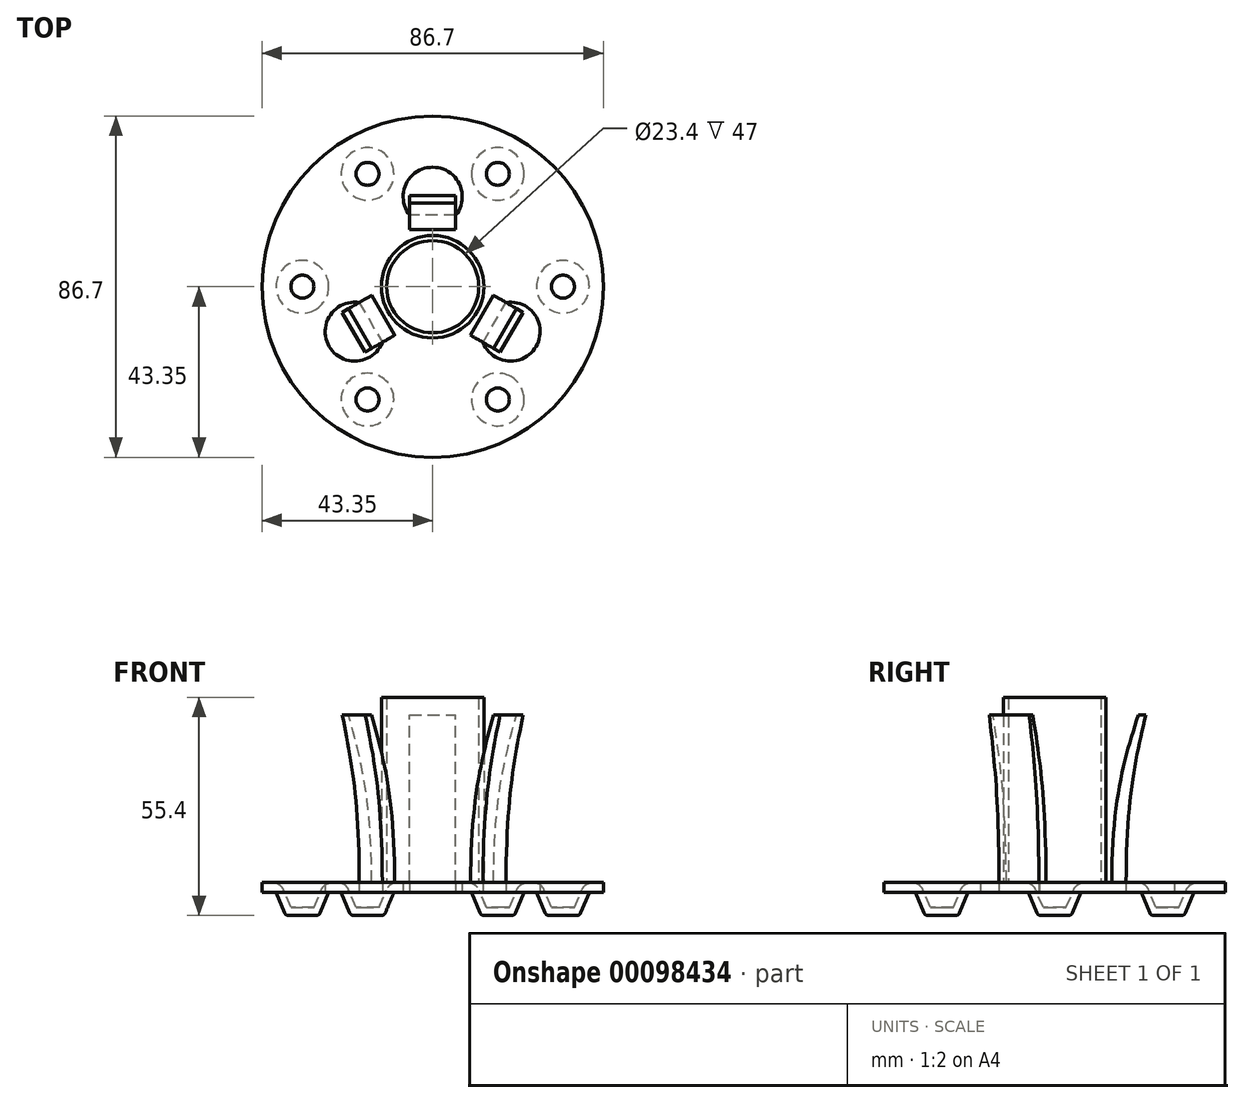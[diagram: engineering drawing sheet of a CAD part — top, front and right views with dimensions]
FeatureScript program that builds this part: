
annotation { "Feature Type Name" : "Feature", "Feature Type Description" : "" }
export const myFeature = defineFeature(function(context is Context, id is Id, definition is map)
    precondition{}
    {
        {
            var Q0;
            Q0=qCreatedBy(makeId("Top.planeOp"),FACE);
            var sketch = newSketch(context, id + "F0", { "sketchPlane" : qUnion([Q0])});
            skCircle(sketch, "E0", {"center": v(0, 0) * mm, "radius": 43.35 * mm});
            skCircle(sketch, "E1", {"center": v(-16.55, -28.67) * mm, "radius": 7.75 * mm});
            skCircle(sketch, "E2", {"center": v(-16.55, -28.67) * mm, "radius": 4.25 * mm});
            skCircle(sketch, "E3.1.0", {"center": v(16.55, -28.67) * mm, "radius": 4.25 * mm});
            skCircle(sketch, "E3.1.1", {"center": v(16.55, -28.67) * mm, "radius": 7.75 * mm});
            skCircle(sketch, "E3.2.0", {"center": v(33.1, 0) * mm, "radius": 4.25 * mm});
            skCircle(sketch, "E3.2.1", {"center": v(33.1, 0) * mm, "radius": 7.75 * mm});
            skCircle(sketch, "E3.3.0", {"center": v(16.55, 28.67) * mm, "radius": 4.25 * mm});
            skCircle(sketch, "E3.3.1", {"center": v(16.55, 28.67) * mm, "radius": 7.75 * mm});
            skCircle(sketch, "E3.4.0", {"center": v(-16.55, 28.67) * mm, "radius": 4.25 * mm});
            skCircle(sketch, "E3.4.1", {"center": v(-16.55, 28.67) * mm, "radius": 7.75 * mm});
            skCircle(sketch, "E3.5.0", {"center": v(-33.1, 0) * mm, "radius": 4.25 * mm});
            skCircle(sketch, "E3.5.1", {"center": v(-33.1, 0) * mm, "radius": 7.75 * mm});
            skCircle(sketch, "E4", {"center": v(19.79, -11.42) * mm, "radius": 7.5 * mm});
            skLineSegment(sketch, "E5", {"start": v(12.8, -14.14) * mm, "end": v(18.64, -4.01) * mm});
            skLineSegment(sketch, "E6", {"start": v(0, 0) * mm, "end": v(37.54, -21.67) * mm, "construction": true});
            skCircle(sketch, "E7.1.0", {"center": v(0, 22.85) * mm, "radius": 7.5 * mm});
            skLineSegment(sketch, "E7.1.1", {"start": v(5.84, 18.15) * mm, "end": v(-5.84, 18.15) * mm});
            skLineSegment(sketch, "E7.1.2", {"start": v(0, 0) * mm, "end": v(0, 43.35) * mm, "construction": true});
            skCircle(sketch, "E7.2.0", {"center": v(-19.79, -11.42) * mm, "radius": 7.5 * mm});
            skLineSegment(sketch, "E7.2.1", {"start": v(-18.64, -4.01) * mm, "end": v(-12.8, -14.14) * mm});
            skLineSegment(sketch, "E7.2.2", {"start": v(0, 0) * mm, "end": v(-37.54, -21.68) * mm, "construction": true});
            skCircle(sketch, "E8.0", {"center": v(-16.55, -28.67) * mm, "radius": 5.75 * mm});
            skCircle(sketch, "E9.1.0", {"center": v(16.55, -28.67) * mm, "radius": 5.75 * mm});
            skCircle(sketch, "E9.2.0", {"center": v(33.1, 0) * mm, "radius": 5.75 * mm});
            skCircle(sketch, "E9.3.0", {"center": v(16.55, 28.67) * mm, "radius": 5.75 * mm});
            skCircle(sketch, "E9.4.0", {"center": v(-16.55, 28.67) * mm, "radius": 5.75 * mm});
            skCircle(sketch, "E9.5.0", {"center": v(-33.1, 0) * mm, "radius": 5.75 * mm});
            skSolve(sketch);
        }
        {
            var Q0;
            Q0=makeQuery(id+"F0.imprint","IMPRINT",FACE,{"disambiguationData":[TD([[makeQuery(id+"F0.imprint","IMPRINT",EDGE,{"derivedFrom":sQuery(id+"F0.wireOp",EDGE,"E0")}),1.0]])]});
            var Q1;
            Q1=makeQuery(id+"F0.imprint","IMPRINT",FACE,{"disambiguationData":[TD([[makeQuery(id+"F0.imprint","IMPRINT",EDGE,{"derivedFrom":sQuery(id+"F0.wireOp",EDGE,"E3.5.1")}),1.0]])]});
            var Q2;
            Q2=makeQuery(id+"F0.imprint","IMPRINT",FACE,{"disambiguationData":[TD([[makeQuery(id+"F0.imprint","IMPRINT",EDGE,{"derivedFrom":sQuery(id+"F0.wireOp",EDGE,"E3.4.1")}),1.0]])]});
            var Q3;
            Q3=makeQuery(id+"F0.imprint","IMPRINT",FACE,{"disambiguationData":[TD([[makeQuery(id+"F0.imprint","IMPRINT",EDGE,{"derivedFrom":sQuery(id+"F0.wireOp",EDGE,"E3.3.1")}),1.0]])]});
            var Q4;
            {var subQ0=sQuery(id+"F0.wireOp",EDGE,"E7.1.1");Q4=makeQuery(id+"F0.imprint","IMPRINT",FACE,{"disambiguationData":[TD([[makeQuery(id+"F0.imprint","IMPRINT",EDGE,{"derivedFrom":subQ0}),1.0]])]});}
            var Q5;
            {var subQ0=sQuery(id+"F0.wireOp",EDGE,"E7.2.1");Q5=makeQuery(id+"F0.imprint","IMPRINT",FACE,{"disambiguationData":[TD([[makeQuery(id+"F0.imprint","IMPRINT",EDGE,{"derivedFrom":subQ0}),1.0]])]});}
            var Q6;
            {var subQ0=sQuery(id+"F0.wireOp",EDGE,"E5");Q6=makeQuery(id+"F0.imprint","IMPRINT",FACE,{"disambiguationData":[TD([[makeQuery(id+"F0.imprint","IMPRINT",EDGE,{"derivedFrom":subQ0}),1.0]])]});}
            var Q7;
            Q7=makeQuery(id+"F0.imprint","IMPRINT",FACE,{"disambiguationData":[TD([[makeQuery(id+"F0.imprint","IMPRINT",EDGE,{"derivedFrom":sQuery(id+"F0.wireOp",EDGE,"E3.2.1")}),1.0]])]});
            var Q8;
            Q8=makeQuery(id+"F0.imprint","IMPRINT",FACE,{"disambiguationData":[TD([[makeQuery(id+"F0.imprint","IMPRINT",EDGE,{"derivedFrom":sQuery(id+"F0.wireOp",EDGE,"E3.1.1")}),1.0]])]});
            var Q9;
            Q9=makeQuery(id+"F0.imprint","IMPRINT",FACE,{"disambiguationData":[TD([[makeQuery(id+"F0.imprint","IMPRINT",EDGE,{"derivedFrom":sQuery(id+"F0.wireOp",EDGE,"E1")}),1.0]])]});
            extrude(context, id + "F1", {"entities" : qUnion([Q0, Q1, Q2, Q3, Q4, Q5, Q6, Q7, Q8, Q9]), "depth" : 2.54 * mm});
        }
        {
            var Q0;
            Q0=makeQuery(id+"F1.opExtrude","CAP_FACE",FACE,{"disambiguationData":[OSD([sQuery(id+"F0.wireOp",EDGE,"E0"),sQuery(id+"F0.wireOp",EDGE,"E4"),sQuery(id+"F0.wireOp",EDGE,"E5"),sQuery(id+"F0.wireOp",EDGE,"E7.1.0"),sQuery(id+"F0.wireOp",EDGE,"E7.1.1"),sQuery(id+"F0.wireOp",EDGE,"E7.2.0"),sQuery(id+"F0.wireOp",EDGE,"E7.2.1"),sQuery(id+"F0.wireOp",EDGE,"E8.0"),sQuery(id+"F0.wireOp",EDGE,"E9.1.0"),sQuery(id+"F0.wireOp",EDGE,"E9.2.0"),sQuery(id+"F0.wireOp",EDGE,"E9.3.0"),sQuery(id+"F0.wireOp",EDGE,"E9.4.0"),sQuery(id+"F0.wireOp",EDGE,"E9.5.0")])],"isStart":false});
            cPlane(context, id + "F2", {"entities" : qUnion([Q0]), "cplaneType" : CPlaneType.OFFSET, "offset" : 0 * mm, "width" : 150 * mm, "height" : 150 * mm});
        }
        {
            var Q0;
            Q0=qCreatedBy(id+"F2.planeOp",FACE);
            var sketch = newSketch(context, id + "F3", { "sketchPlane" : qUnion([Q0])});
            skCircle(sketch, "E10.0", {"center": v(-16.55, -28.67) * mm, "radius": 7.75 * mm});
            skSolve(sketch);
        }
        {
            var Q0;
            Q0=makeQuery(id+"F1.opExtrude","CAP_FACE",FACE,{"disambiguationData":[OSD([sQuery(id+"F0.wireOp",EDGE,"E0"),sQuery(id+"F0.wireOp",EDGE,"E4"),sQuery(id+"F0.wireOp",EDGE,"E5"),sQuery(id+"F0.wireOp",EDGE,"E7.1.0"),sQuery(id+"F0.wireOp",EDGE,"E7.1.1"),sQuery(id+"F0.wireOp",EDGE,"E7.2.0"),sQuery(id+"F0.wireOp",EDGE,"E7.2.1"),sQuery(id+"F0.wireOp",EDGE,"E8.0"),sQuery(id+"F0.wireOp",EDGE,"E9.1.0"),sQuery(id+"F0.wireOp",EDGE,"E9.2.0"),sQuery(id+"F0.wireOp",EDGE,"E9.3.0"),sQuery(id+"F0.wireOp",EDGE,"E9.4.0"),sQuery(id+"F0.wireOp",EDGE,"E9.5.0")])],"isStart":false});
            cPlane(context, id + "F4", {"entities" : qUnion([Q0]), "cplaneType" : CPlaneType.OFFSET, "offset" : 8.4 * mm, "oppositeDirection" : true, "width" : 150 * mm, "height" : 150 * mm});
        }
        {
            var Q0;
            Q0=qCreatedBy(id+"F4.planeOp",FACE);
            var sketch = newSketch(context, id + "F5", { "sketchPlane" : qUnion([Q0])});
            skCircle(sketch, "E11.0", {"center": v(-33.1, 0) * mm, "radius": 4.25 * mm});
            skCircle(sketch, "E12.0", {"center": v(-16.55, 28.67) * mm, "radius": 4.25 * mm});
            skCircle(sketch, "E12.1", {"center": v(16.55, 28.67) * mm, "radius": 4.25 * mm});
            skCircle(sketch, "E12.2", {"center": v(33.1, 0) * mm, "radius": 4.25 * mm});
            skCircle(sketch, "E12.3", {"center": v(16.55, -28.67) * mm, "radius": 4.25 * mm});
            skCircle(sketch, "E12.4", {"center": v(-16.55, -28.67) * mm, "radius": 4.25 * mm});
            skSolve(sketch);
        }
        {
            var Q1;
            Q1=makeQuery(id+"F3.imprint","IMPRINT",FACE,{"disambiguationData":[TD([[makeQuery(id+"F3.imprint","IMPRINT",EDGE,{"derivedFrom":sQuery(id+"F3.wireOp",EDGE,"E10.0")}),1.0]])]});
            var Q2;
            Q2=makeQuery(id+"F5.imprint","IMPRINT",FACE,{"disambiguationData":[TD([[makeQuery(id+"F5.imprint","IMPRINT",EDGE,{"derivedFrom":sQuery(id+"F5.wireOp",EDGE,"E12.4")}),1.0]])]});
            loft(context, id + "F6", {"sheetProfilesArray" : [{ "sheetProfileEntities" : qUnion([Q1]) }, { "sheetProfileEntities" : qUnion([Q2]) }]});
        }
        {
            var Q0;
            Q0=makeQuery(id+"F6.opLoft","CAP_FACE",FACE,{"disambiguationData":[OSD([makeQuery(id+"F3.imprint","IMPRINT",FACE,{"disambiguationData":[TD([[makeQuery(id+"F3.imprint","IMPRINT",EDGE,{"derivedFrom":sQuery(id+"F3.wireOp",EDGE,"E10.0")}),1.0]])]})])],"isStart":true});
            shell(context, id + "F7", {"entities" : qUnion([Q0]), "thickness" : 2 * mm});
        }
        {
            var Q0;
            Q0=makeQuery(id+"F7.opShell","OFFSET_EDGE",EDGE,{"disambiguationData":[OSD([sQuery(id+"F3.wireOp",EDGE,"E10.0")])]});
            fillet(context, id + "F8", {"entities" : qUnion([Q0]), "radius" : 3.2 * mm, "tangentPropagation" : true, "allowEdgeOverflow" : false});
        }
        {
            var Q0;
            Q0=makeQuery(id+"F1.opExtrude","CAP_EDGE",EDGE,{"disambiguationData":[OSD([sQuery(id+"F0.wireOp",EDGE,"E8.0")])],"isStart":false});
            var Q1;
            Q1=makeQuery(id+"F1.opExtrude","CAP_EDGE",EDGE,{"disambiguationData":[OSD([sQuery(id+"F0.wireOp",EDGE,"E9.5.0")])],"isStart":false});
            var Q2;
            Q2=makeQuery(id+"F1.opExtrude","CAP_EDGE",EDGE,{"disambiguationData":[OSD([sQuery(id+"F0.wireOp",EDGE,"E9.1.0")])],"isStart":false});
            var Q3;
            Q3=makeQuery(id+"F1.opExtrude","CAP_EDGE",EDGE,{"disambiguationData":[OSD([sQuery(id+"F0.wireOp",EDGE,"E9.2.0")])],"isStart":false});
            var Q4;
            Q4=makeQuery(id+"F1.opExtrude","CAP_EDGE",EDGE,{"disambiguationData":[OSD([sQuery(id+"F0.wireOp",EDGE,"E9.3.0")])],"isStart":false});
            var Q5;
            Q5=makeQuery(id+"F1.opExtrude","CAP_EDGE",EDGE,{"disambiguationData":[OSD([sQuery(id+"F0.wireOp",EDGE,"E9.4.0")])],"isStart":false});
            fillet(context, id + "F9", {"entities" : qUnion([Q0, Q1, Q2, Q3, Q4, Q5]), "radius" : 2 * mm, "tangentPropagation" : true, "allowEdgeOverflow" : false});
        }
        {
            var Q0;
            Q0=makeQuery(id+"F6.opLoft","MID_CAP_EDGE",EDGE,{"disambiguationData":[OSD([sQuery(id+"F3.wireOp",EDGE,"E10.0"),sQuery(id+"F5.wireOp",EDGE,"E12.4")])],"capPos":1.0});
            fillet(context, id + "F10", {"entities" : qUnion([Q0]), "radius" : 1 * mm, "tangentPropagation" : true, "allowEdgeOverflow" : false});
        }
        {
            var Q0;
            Q0=qCreatedBy(makeId("Front.planeOp"),FACE);
            var sketch = newSketch(context, id + "F11", { "sketchPlane" : qUnion([Q0])});
            skLineSegment(sketch, "E13", {"start": v(0, 0) * mm, "end": v(0, 21.76) * mm});
            skSolve(sketch);
        }
        {
            var Q0;
            Q0=makeQuery(id+"F6.opLoft","SWEPT_BODY",BODY,{"disambiguationData":[OSD([makeQuery(id+"F3.imprint","IMPRINT",FACE,{"disambiguationData":[TD([[makeQuery(id+"F3.imprint","IMPRINT",EDGE,{"derivedFrom":sQuery(id+"F3.wireOp",EDGE,"E10.0")}),1.0]])]}),makeQuery(id+"F5.imprint","IMPRINT",FACE,{"disambiguationData":[TD([[makeQuery(id+"F5.imprint","IMPRINT",EDGE,{"derivedFrom":sQuery(id+"F5.wireOp",EDGE,"E12.4")}),1.0]])]})])]});
            var Q1;
            Q1=sQuery(id+"F11.wireOp",EDGE,"E13");
            circularPattern(context, id + "F12", {"entities" : qUnion([Q0]), "axis" : qUnion([Q1]), "angle" : 60 * degree, "instanceCount" : 6});
        }
        {
            var Q0;
            Q0=makeQuery(id+"F1.opExtrude","SWEPT_BODY",BODY,{"disambiguationData":[OSD([sQuery(id+"F0.wireOp",EDGE,"E0"),sQuery(id+"F0.wireOp",EDGE,"E4"),sQuery(id+"F0.wireOp",EDGE,"E5"),sQuery(id+"F0.wireOp",EDGE,"E7.1.0"),sQuery(id+"F0.wireOp",EDGE,"E7.1.1"),sQuery(id+"F0.wireOp",EDGE,"E7.2.0"),sQuery(id+"F0.wireOp",EDGE,"E7.2.1"),sQuery(id+"F0.wireOp",EDGE,"E8.0"),sQuery(id+"F0.wireOp",EDGE,"E9.1.0"),sQuery(id+"F0.wireOp",EDGE,"E9.2.0"),sQuery(id+"F0.wireOp",EDGE,"E9.3.0"),sQuery(id+"F0.wireOp",EDGE,"E9.4.0"),sQuery(id+"F0.wireOp",EDGE,"E9.5.0")])]});
            var Q1;
            Q1=makeQuery(id+"F6.opLoft","SWEPT_BODY",BODY,{"disambiguationData":[OSD([makeQuery(id+"F3.imprint","IMPRINT",FACE,{"disambiguationData":[TD([[makeQuery(id+"F3.imprint","IMPRINT",EDGE,{"derivedFrom":sQuery(id+"F3.wireOp",EDGE,"E10.0")}),1.0]])]}),makeQuery(id+"F5.imprint","IMPRINT",FACE,{"disambiguationData":[TD([[makeQuery(id+"F5.imprint","IMPRINT",EDGE,{"derivedFrom":sQuery(id+"F5.wireOp",EDGE,"E12.4")}),1.0]])]})])]});
            var Q2;
            Q2=makeQuery(id+"F12.opPattern","COPY",BODY,{"derivedFrom":makeQuery(id+"F6.opLoft","SWEPT_BODY",BODY,{"disambiguationData":[OSD([makeQuery(id+"F3.imprint","IMPRINT",FACE,{"disambiguationData":[TD([[makeQuery(id+"F3.imprint","IMPRINT",EDGE,{"derivedFrom":sQuery(id+"F3.wireOp",EDGE,"E10.0")}),1.0]])]}),makeQuery(id+"F5.imprint","IMPRINT",FACE,{"disambiguationData":[TD([[makeQuery(id+"F5.imprint","IMPRINT",EDGE,{"derivedFrom":sQuery(id+"F5.wireOp",EDGE,"E12.4")}),1.0]])]})])]}),"instanceName":"1"});
            var Q3;
            Q3=makeQuery(id+"F12.opPattern","COPY",BODY,{"derivedFrom":makeQuery(id+"F6.opLoft","SWEPT_BODY",BODY,{"disambiguationData":[OSD([makeQuery(id+"F3.imprint","IMPRINT",FACE,{"disambiguationData":[TD([[makeQuery(id+"F3.imprint","IMPRINT",EDGE,{"derivedFrom":sQuery(id+"F3.wireOp",EDGE,"E10.0")}),1.0]])]}),makeQuery(id+"F5.imprint","IMPRINT",FACE,{"disambiguationData":[TD([[makeQuery(id+"F5.imprint","IMPRINT",EDGE,{"derivedFrom":sQuery(id+"F5.wireOp",EDGE,"E12.4")}),1.0]])]})])]}),"instanceName":"3"});
            var Q4;
            Q4=makeQuery(id+"F12.opPattern","COPY",BODY,{"derivedFrom":makeQuery(id+"F6.opLoft","SWEPT_BODY",BODY,{"disambiguationData":[OSD([makeQuery(id+"F3.imprint","IMPRINT",FACE,{"disambiguationData":[TD([[makeQuery(id+"F3.imprint","IMPRINT",EDGE,{"derivedFrom":sQuery(id+"F3.wireOp",EDGE,"E10.0")}),1.0]])]}),makeQuery(id+"F5.imprint","IMPRINT",FACE,{"disambiguationData":[TD([[makeQuery(id+"F5.imprint","IMPRINT",EDGE,{"derivedFrom":sQuery(id+"F5.wireOp",EDGE,"E12.4")}),1.0]])]})])]}),"instanceName":"5"});
            var Q5;
            Q5=makeQuery(id+"F12.opPattern","COPY",BODY,{"derivedFrom":makeQuery(id+"F6.opLoft","SWEPT_BODY",BODY,{"disambiguationData":[OSD([makeQuery(id+"F3.imprint","IMPRINT",FACE,{"disambiguationData":[TD([[makeQuery(id+"F3.imprint","IMPRINT",EDGE,{"derivedFrom":sQuery(id+"F3.wireOp",EDGE,"E10.0")}),1.0]])]}),makeQuery(id+"F5.imprint","IMPRINT",FACE,{"disambiguationData":[TD([[makeQuery(id+"F5.imprint","IMPRINT",EDGE,{"derivedFrom":sQuery(id+"F5.wireOp",EDGE,"E12.4")}),1.0]])]})])]}),"instanceName":"2"});
            var Q6;
            Q6=makeQuery(id+"F12.opPattern","COPY",BODY,{"derivedFrom":makeQuery(id+"F6.opLoft","SWEPT_BODY",BODY,{"disambiguationData":[OSD([makeQuery(id+"F3.imprint","IMPRINT",FACE,{"disambiguationData":[TD([[makeQuery(id+"F3.imprint","IMPRINT",EDGE,{"derivedFrom":sQuery(id+"F3.wireOp",EDGE,"E10.0")}),1.0]])]}),makeQuery(id+"F5.imprint","IMPRINT",FACE,{"disambiguationData":[TD([[makeQuery(id+"F5.imprint","IMPRINT",EDGE,{"derivedFrom":sQuery(id+"F5.wireOp",EDGE,"E12.4")}),1.0]])]})])]}),"instanceName":"4"});
            booleanBodies(context, id + "F13", {"operationType" : BooleanOperationType.UNION, "tools" : qUnion([Q0, Q1, Q2, Q3, Q4, Q5, Q6])});
        }
        {
            var Q0;
            {var subQ0=makeQuery(id+"F6.opLoft","CAP_FACE",FACE,{"disambiguationData":[OSD([makeQuery(id+"F3.imprint","IMPRINT",FACE,{"disambiguationData":[TD([[makeQuery(id+"F3.imprint","IMPRINT",EDGE,{"derivedFrom":sQuery(id+"F3.wireOp",EDGE,"E10.0")}),1.0]])]})])],"isStart":true});Q0=makeQuery(id+"F13.opBoolean","MERGE",FACE,{"derivedFrom":[subQ0,makeQuery(id+"F1.opExtrude","CAP_FACE",FACE,{"disambiguationData":[OSD([sQuery(id+"F0.wireOp",EDGE,"E0"),sQuery(id+"F0.wireOp",EDGE,"E4"),sQuery(id+"F0.wireOp",EDGE,"E5"),sQuery(id+"F0.wireOp",EDGE,"E7.1.0"),sQuery(id+"F0.wireOp",EDGE,"E7.1.1"),sQuery(id+"F0.wireOp",EDGE,"E7.2.0"),sQuery(id+"F0.wireOp",EDGE,"E7.2.1"),sQuery(id+"F0.wireOp",EDGE,"E8.0"),sQuery(id+"F0.wireOp",EDGE,"E9.1.0"),sQuery(id+"F0.wireOp",EDGE,"E9.2.0"),sQuery(id+"F0.wireOp",EDGE,"E9.3.0"),sQuery(id+"F0.wireOp",EDGE,"E9.4.0"),sQuery(id+"F0.wireOp",EDGE,"E9.5.0")])],"isStart":false}),makeQuery(id+"F12.opPattern","COPY",FACE,{"derivedFrom":subQ0,"instanceName":"1"}),makeQuery(id+"F12.opPattern","COPY",FACE,{"derivedFrom":subQ0,"instanceName":"2"}),makeQuery(id+"F12.opPattern","COPY",FACE,{"derivedFrom":subQ0,"instanceName":"3"}),makeQuery(id+"F12.opPattern","COPY",FACE,{"derivedFrom":subQ0,"instanceName":"4"}),makeQuery(id+"F12.opPattern","COPY",FACE,{"derivedFrom":subQ0,"instanceName":"5"})]});}
            var sketch = newSketch(context, id + "F14", { "sketchPlane" : qUnion([Q0])});
            skCircle(sketch, "E14", {"center": v(0, 0) * mm, "radius": 13 * mm});
            skCircle(sketch, "E15.0", {"center": v(0, 0) * mm, "radius": 11.7 * mm});
            skSolve(sketch);
        }
        {
            var Q0;
            Q0 = qSketchRegion(id + "F14", true);
            extrude(context, id + "F15", {"entities" : qUnion([Q0]), "operationType" : NewBodyOperationType.ADD, "depth" : 47 * mm});
        }
        {
            var Q0;
            {var subQ0=sQuery(id+"F3.wireOp",EDGE,"E10.0");var subQ2=sQuery(id+"F0.wireOp",EDGE,"E7.2.0");var subQ3=sQuery(id+"F0.wireOp",EDGE,"E7.2.1");var subQ4=sQuery(id+"F0.wireOp",EDGE,"E7.1.1");var subQ5=sQuery(id+"F0.wireOp",EDGE,"E0");var subQ6=sQuery(id+"F0.wireOp",EDGE,"E4");var subQ7=sQuery(id+"F0.wireOp",EDGE,"E5");var subQ8=sQuery(id+"F0.wireOp",EDGE,"E7.1.0");var subQ9=makeQuery(id+"F6.opLoft","CAP_FACE",FACE,{"disambiguationData":[OSD([makeQuery(id+"F3.imprint","IMPRINT",FACE,{"disambiguationData":[TD([[makeQuery(id+"F3.imprint","IMPRINT",EDGE,{"derivedFrom":subQ0}),1.0]])]})])],"isStart":true});Q0=makeQuery(id+"F15.boolean.opBoolean","SPLIT",FACE,{"disambiguationData":[TD([makeQuery(id+"F1.opExtrude","SWEPT_FACE",FACE,{"disambiguationData":[OSD([subQ5])]})])],"derivedFrom":makeQuery(id+"F13.opBoolean","MERGE",FACE,{"derivedFrom":[subQ9,makeQuery(id+"F1.opExtrude","CAP_FACE",FACE,{"disambiguationData":[OSD([subQ5,subQ6,subQ7,subQ8,subQ4,subQ2,subQ3,sQuery(id+"F0.wireOp",EDGE,"E8.0"),sQuery(id+"F0.wireOp",EDGE,"E9.1.0"),sQuery(id+"F0.wireOp",EDGE,"E9.2.0"),sQuery(id+"F0.wireOp",EDGE,"E9.3.0"),sQuery(id+"F0.wireOp",EDGE,"E9.4.0"),sQuery(id+"F0.wireOp",EDGE,"E9.5.0")])],"isStart":false}),makeQuery(id+"F12.opPattern","COPY",FACE,{"derivedFrom":subQ9,"instanceName":"1"}),makeQuery(id+"F12.opPattern","COPY",FACE,{"derivedFrom":subQ9,"instanceName":"2"}),makeQuery(id+"F12.opPattern","COPY",FACE,{"derivedFrom":subQ9,"instanceName":"3"}),makeQuery(id+"F12.opPattern","COPY",FACE,{"derivedFrom":subQ9,"instanceName":"4"}),makeQuery(id+"F12.opPattern","COPY",FACE,{"derivedFrom":subQ9,"instanceName":"5"})]})});}
            var sketch = newSketch(context, id + "F16", { "sketchPlane" : qUnion([Q0])});
            skLineSegment(sketch, "E16.bottom", {"start": v(-5.84, 18.15) * mm, "end": v(5.84, 18.15) * mm});
            skLineSegment(sketch, "E16.top", {"start": v(-5.84, 14.5) * mm, "end": v(5.84, 14.5) * mm});
            skLineSegment(sketch, "E16.left", {"start": v(-5.84, 18.15) * mm, "end": v(-5.84, 14.5) * mm});
            skLineSegment(sketch, "E16.right", {"start": v(5.84, 18.15) * mm, "end": v(5.84, 14.5) * mm});
            skSolve(sketch);
        }
        {
            var Q0;
            Q0=makeQuery(id+"F16.imprint","IMPRINT",FACE,{"disambiguationData":[TD([[makeQuery(id+"F16.imprint","IMPRINT",EDGE,{"derivedFrom":sQuery(id+"F16.wireOp",EDGE,"E16.top")}),-1.0]])]});
            cPlane(context, id + "F17", {"entities" : qUnion([Q0]), "cplaneType" : CPlaneType.OFFSET, "offset" : 42.5 * mm, "width" : 150 * mm, "height" : 150 * mm});
        }
        {
            var Q0;
            Q0=qCreatedBy(id+"F17.planeOp",FACE);
            var sketch = newSketch(context, id + "F18", { "sketchPlane" : qUnion([Q0])});
            skLineSegment(sketch, "E17.0.0", {"start": v(-5.84, 18.15) * mm, "end": v(-5.84, 14.5) * mm, "construction": true});
            skLineSegment(sketch, "E17.0.1", {"start": v(-5.84, 14.5) * mm, "end": v(5.84, 14.5) * mm, "construction": true});
            skLineSegment(sketch, "E17.0.2", {"start": v(5.84, 14.5) * mm, "end": v(5.84, 18.15) * mm, "construction": true});
            skLineSegment(sketch, "E17.0.3", {"start": v(5.84, 18.15) * mm, "end": v(-5.84, 18.15) * mm, "construction": true});
            skLineSegment(sketch, "E18", {"start": v(5.84, 23.15) * mm, "end": v(-5.84, 23.15) * mm});
            skLineSegment(sketch, "E19", {"start": v(-5.84, 23.15) * mm, "end": v(-5.84, 21.25) * mm});
            skLineSegment(sketch, "E20", {"start": v(-5.84, 21.25) * mm, "end": v(5.84, 21.25) * mm});
            skLineSegment(sketch, "E21", {"start": v(5.84, 21.25) * mm, "end": v(5.84, 23.15) * mm});
            skSolve(sketch);
        }
        {
            var Q1;
            Q1=makeQuery(id+"F16.imprint","IMPRINT",FACE,{"disambiguationData":[TD([[makeQuery(id+"F16.imprint","IMPRINT",EDGE,{"derivedFrom":sQuery(id+"F16.wireOp",EDGE,"E16.bottom")}),1.0]])]});
            var Q2;
            Q2=makeQuery(id+"F18.imprint","IMPRINT",FACE,{"disambiguationData":[TD([[makeQuery(id+"F18.imprint","IMPRINT",EDGE,{"derivedFrom":sQuery(id+"F18.wireOp",EDGE,"E18")}),1.0]])]});
            loft(context, id + "F19", {"startCondition" : LoftEndDerivativeType.NORMAL_TO_PROFILE, "startMagnitude" : 1.5, "sheetProfilesArray" : [{ "sheetProfileEntities" : qUnion([Q1]) }, { "sheetProfileEntities" : qUnion([Q2]) }]});
        }
        {
            var Q0;
            Q0=makeQuery(id+"F19.opLoft","SWEPT_BODY",BODY,{"disambiguationData":[OSD([makeQuery(id+"F16.imprint","IMPRINT",FACE,{"disambiguationData":[TD([[makeQuery(id+"F16.imprint","IMPRINT",EDGE,{"derivedFrom":sQuery(id+"F16.wireOp",EDGE,"E16.bottom")}),1.0]])]}),makeQuery(id+"F18.imprint","IMPRINT",FACE,{"disambiguationData":[TD([[makeQuery(id+"F18.imprint","IMPRINT",EDGE,{"derivedFrom":sQuery(id+"F18.wireOp",EDGE,"E18")}),1.0]])]})])]});
            var Q1;
            Q1=sQuery(id+"F11.wireOp",EDGE,"E13");
            circularPattern(context, id + "F20", {"operationType" : NewBodyOperationType.ADD, "entities" : qUnion([Q0]), "axis" : qUnion([Q1]), "angle" : 120 * degree, "instanceCount" : 3});
        }
    });
